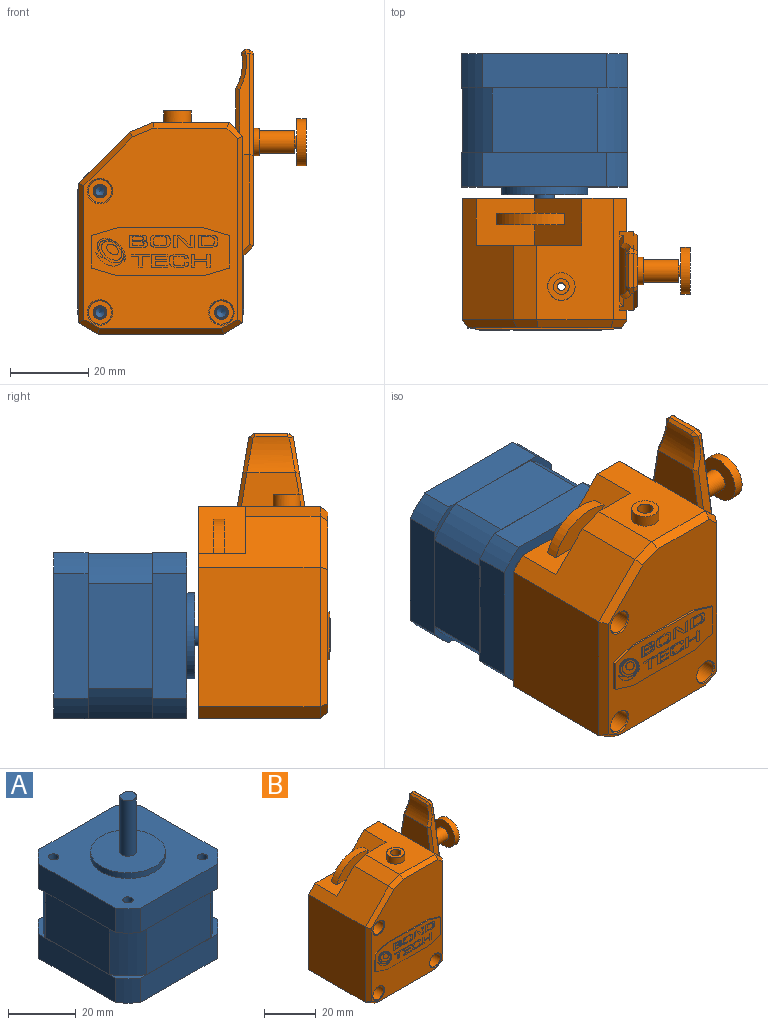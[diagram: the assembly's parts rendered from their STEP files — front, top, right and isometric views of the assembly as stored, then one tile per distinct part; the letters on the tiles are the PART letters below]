
ASSEMBLY  parts=2 mates=1
PART A: 50 faces, bbox 42.4x42.4x56 mm
  f0: cylinder r=2.5mm len=20mm, axis (0,0,-1), area 265.9mm2, adj f1,f2,f29,f30
  f1: plane 5x4.5mm, normal (0,0,1), area 18.6mm2, adj f0,f29
  f2: plane 22x22mm, normal (0,0,1), area 360.5mm2, adj f0,f3
  f3: cylinder r=11mm len=22mm, axis (0,0,-1), area 138.2mm2, adj f2,f8
  f4: plane 31.78x8.75mm, normal (1,0,0), area 278mm2, adj f8,f9,f10,f32
  f5: plane 31.78x8.75mm, normal (0,-1,0), area 278mm2, adj f8,f9,f11,f32
  f6: plane 31.78x8.75mm, normal (-1,0,0), area 278mm2, adj f8,f11,f12,f32
  f7: plane 31.78x8.75mm, normal (0,1,0), area 278mm2, adj f8,f10,f12,f32
  f8: plane 42.42x42.42mm, normal (0,0,1), area 1339.6mm2, adj f3,f4,f5,f6,f7,f9,f10,f11
  f9: cylinder r=26.5mm len=8.75mm, axis (0,0,-1), area 66.1mm2, adj f4,f5,f8,f32
  f10: cylinder r=26.5mm len=8.75mm, axis (0,0,-1), area 66.1mm2, adj f4,f7,f8,f32
  f11: cylinder r=26.5mm len=8.75mm, axis (0,0,-1), area 66.1mm2, adj f5,f6,f8,f32
  f12: cylinder r=26.5mm len=8.75mm, axis (0,0,-1), area 66.1mm2, adj f6,f7,f8,f32
  f13: cone r=1.25mm half-angle=59deg, axis (0,0,1), area 5.7mm2, adj f14
  f14: cylinder r=1.25mm len=2.5mm, axis (0,0,1), area 11.8mm2, adj f13,f15
  f15: plane 3x3mm, normal (0,0,1), area 2.2mm2, adj f14,f16
  f16: cylinder r=1.5mm len=6mm, axis (0,0,1), area 56.5mm2, adj f8,f15
  f17: cone r=1.25mm half-angle=59deg, axis (0,0,1), area 5.7mm2, adj f18
  f18: cylinder r=1.25mm len=2.5mm, axis (0,0,1), area 11.8mm2, adj f17,f19
  f19: plane 3x3mm, normal (0,0,1), area 2.2mm2, adj f18,f20
  f20: cylinder r=1.5mm len=6mm, axis (0,0,1), area 56.5mm2, adj f8,f19
  f21: cone r=1.25mm half-angle=59deg, axis (0,0,1), area 5.7mm2, adj f22
  f22: cylinder r=1.25mm len=2.5mm, axis (0,0,1), area 11.8mm2, adj f21,f23
  f23: plane 3x3mm, normal (0,0,1), area 2.2mm2, adj f22,f24
  f24: cylinder r=1.5mm len=6mm, axis (0,0,1), area 56.5mm2, adj f8,f23
  f25: cone r=1.25mm half-angle=59deg, axis (0,0,1), area 5.7mm2, adj f26
  f26: cylinder r=1.25mm len=2.5mm, axis (0,0,1), area 11.8mm2, adj f25,f27
  f27: plane 3x3mm, normal (0,0,1), area 2.2mm2, adj f26,f28
  f28: cylinder r=1.5mm len=6mm, axis (0,0,1), area 56.5mm2, adj f8,f27
  f29: plane 15x3mm, normal (0,1,0), area 45mm2, adj f0,f1,f30
  f30: plane 3x0.5mm, normal (0,0,1), area 1mm2, adj f0,f29
  f31: plane 42.42x42.42mm, normal (0,0,1), area 67.2mm2, adj f33,f34,f35,f36,f37,f38,f39,f40
  f32: plane 42.42x42.42mm, normal (0,0,-1), area 67.2mm2, adj f4,f5,f6,f7,f9,f10,f11,f12
  f33: cylinder r=25mm len=16.5mm, axis (0,0,1), area 181.5mm2, adj f31,f32,f34,f40
  f34: plane 26.79x16.5mm, normal (0,1,0), area 442mm2, adj f31,f32,f33,f35
  f35: cylinder r=25mm len=16.5mm, axis (0,0,1), area 181.5mm2, adj f31,f32,f34,f36
  f36: plane 26.79x16.5mm, normal (1,0,0), area 442mm2, adj f31,f32,f35,f37
  f37: cylinder r=25mm len=16.5mm, axis (0,0,1), area 181.5mm2, adj f31,f32,f36,f38
  f38: plane 26.79x16.5mm, normal (0,-1,0), area 442mm2, adj f31,f32,f37,f39
  f39: cylinder r=25mm len=16.5mm, axis (0,0,1), area 181.5mm2, adj f31,f32,f38,f40
  f40: plane 26.79x16.5mm, normal (-1,0,0), area 442mm2, adj f31,f32,f33,f39
  f41: plane 42.42x42.42mm, normal (0,0,-1), area 1748.1mm2, adj f42,f43,f44,f45,f46,f47,f48,f49
  f42: cylinder r=26.5mm len=8.75mm, axis (0,0,-1), area 66.1mm2, adj f31,f41,f48,f49
  f43: cylinder r=26.5mm len=8.75mm, axis (0,0,-1), area 66.1mm2, adj f31,f41,f47,f48
  f44: cylinder r=26.5mm len=8.75mm, axis (0,0,-1), area 66.1mm2, adj f31,f41,f46,f47
  f45: cylinder r=26.5mm len=8.75mm, axis (0,0,-1), area 66.1mm2, adj f31,f41,f46,f49
  f46: plane 31.78x8.75mm, normal (0,1,0), area 278mm2, adj f31,f41,f44,f45
  f47: plane 31.78x8.75mm, normal (-1,0,0), area 278mm2, adj f31,f41,f43,f44
  f48: plane 31.78x8.75mm, normal (0,-1,0), area 278mm2, adj f31,f41,f42,f43
  f49: plane 31.78x8.75mm, normal (1,0,0), area 278mm2, adj f31,f41,f42,f45
PART B: 276 faces, bbox 58.2x33.6x72.9 mm
  f0: cone r=3mm half-angle=45deg, axis (0,-1,0), area 6.9mm2, adj f4,f23
  f1: cone r=3mm half-angle=45deg, axis (0,-1,0), area 6.9mm2, adj f3,f23
  f2: cone r=3mm half-angle=45deg, axis (0,-1,0), area 6.9mm2, adj f5,f23
  f3: cylinder r=3mm len=6mm, axis (0,-1,0), area 80.1mm2, adj f1,f92
  f4: cylinder r=3mm len=6mm, axis (0,-1,0), area 80.1mm2, adj f0,f91
  f5: cylinder r=3mm len=6mm, axis (0,-1,0), area 80.1mm2, adj f2,f90
  f6: cylinder r=11mm len=22mm, axis (0,1,0), area 138.2mm2, adj f29,f89
  f7: cylinder r=1.75mm len=10.5mm, axis (-1,0,0), area 115.5mm2, adj f85,f88
  f8: cylinder r=1.5mm len=11mm, axis (-1,0,0), area 103.7mm2, adj f87,f88
  f9: cylinder r=6mm len=12mm, axis (-1,0,0), area 94.2mm2, adj f86,f87
  f10: cylinder r=2.88mm len=9mm, axis (-1,0,0), area 162.6mm2, adj f84,f85
  f11: cylinder r=3.5mm len=7mm, axis (-1,0,0), area 33mm2, adj f56,f84
  f12: cylinder r=2mm len=4mm, axis (0,0,-1), area 37.7mm2, adj f22,f52
  f13: cylinder r=3.5mm len=7mm, axis (0,0,-1), area 66mm2, adj f27,f52
  f14: cylinder r=1mm len=51mm, axis (0,0,-1), area 320.4mm2, adj f22,f51
  f15: cylinder r=8mm len=16mm, axis (0,0,-1), area 150.8mm2, adj f25,f51
  f16: cylinder r=1.75mm len=28.5mm, axis (0,1,0), area 313.4mm2, adj f29,f90
  f17: cylinder r=1.75mm len=28.5mm, axis (0,1,0), area 313.4mm2, adj f29,f91
  f18: cylinder r=1.75mm len=28.5mm, axis (0,1,0), area 313.4mm2, adj f29,f92
  f19: plane 35.32x12.32mm, normal (0,-1,0), area 302.9mm2, adj f43,f44,f45,f46,f47,f48,f49,f50
  f20: plane 15x12mm, normal (0,0,1), area 150.6mm2, adj f21,f28,f29,f93,f94,f95,f96
  f21: plane 12x12mm, normal (-0.71,0,0.71), area 171.1mm2, adj f20,f27,f29,f93,f94,f95,f96
  f22: plane 4x4mm, normal (0,0,1), area 9.4mm2, adj f12,f14
  f23: plane 51.2x39.2mm, normal (0,-1,0), area 1375.8mm2, adj f0,f1,f2,f34,f35,f36,f37,f38
  f24: plane 35.61x31mm, normal (-1,0,0), area 1104mm2, adj f28,f29,f33,f40
  f25: plane 32x31mm, normal (0,0,-1), area 790.9mm2, adj f15,f29,f32,f33,f41
  f26: plane 47.61x31mm, normal (1,0,0), area 863.4mm2, adj f29,f30,f32,f37,f53,f54,f55,f61
  f27: plane 31x19.5mm, normal (0,0,1), area 428mm2, adj f13,f21,f29,f30,f31,f34,f93
  f28: plane 31x13.03mm, normal (-0.71,0,0.71), area 409.4mm2, adj f20,f24,f29,f31,f38,f93
  f29: plane 54x42mm, normal (0,1,0), area 1538.3mm2, adj f6,f16,f17,f18,f20,f21,f24,f25
  f30: plane 31x3.5mm, normal (0.71,0,0.71), area 104mm2, adj f26,f27,f29,f35,f59,f60,f61,f62
  f31: plane 19x5.98mm, normal (-0.38,0,0.92), area 122.9mm2, adj f27,f28,f36,f93
  f32: plane 31x5mm, normal (0.5,0,-0.87), area 179mm2, adj f25,f26,f29,f39
  f33: plane 31x5mm, normal (-0.5,0,-0.87), area 179mm2, adj f24,f25,f29,f42
  f34: plane 19.5x2mm, normal (0,-0.57,0.82), area 46.6mm2, adj f23,f27,f35,f36
  f35: plane 4.08x4.08mm, normal (0.58,-0.57,0.58), area 10.7mm2, adj f23,f30,f34,f37
  f36: plane 6.25x3.66mm, normal (-0.31,-0.57,0.76), area 15.1mm2, adj f23,f31,f34,f38
  f37: plane 47.61x2mm, normal (0.82,-0.57,0), area 114.6mm2, adj f23,f26,f35,f39
  f38: plane 13.82x13.61mm, normal (-0.58,-0.57,0.58), area 43.9mm2, adj f23,f28,f36,f40
  f39: plane 5.38x3.7mm, normal (0.41,-0.57,-0.71), area 12.7mm2, adj f23,f32,f37,f41
  f40: plane 35.61x2mm, normal (-0.82,-0.57,0), area 85.3mm2, adj f23,f24,f38,f42
  f41: plane 32x2mm, normal (0,-0.57,-0.82), area 77.2mm2, adj f23,f25,f39,f42
  f42: plane 5.38x3.7mm, normal (-0.41,-0.57,-0.71), area 12.7mm2, adj f23,f33,f40,f41
  f43: plane 6.66x2mm, normal (-0.29,0,-0.96), area 3.5mm2, adj f19,f23,f44,f50
  f44: plane 21.99x0.5mm, normal (0,0,-1), area 11mm2, adj f19,f23,f43,f45
  f45: plane 6.66x2mm, normal (0.29,0,-0.96), area 3.5mm2, adj f19,f23,f44,f46
  f46: plane 8.3x0.5mm, normal (1,0,0), area 4.2mm2, adj f19,f23,f45,f47
  f47: plane 6.66x2mm, normal (0.29,0,0.96), area 3.5mm2, adj f19,f23,f46,f48
  f48: plane 21.99x0.5mm, normal (0,0,1), area 11mm2, adj f19,f23,f47,f49
  f49: plane 6.66x2mm, normal (-0.29,0,0.96), area 3.5mm2, adj f19,f23,f48,f50
  f50: plane 8.3x0.5mm, normal (-1,0,0), area 4.2mm2, adj f19,f23,f43,f49
  f51: plane 16x16mm, normal (0,0,-1), area 197.9mm2, adj f14,f15
  f52: plane 7x7mm, normal (0,0,1), area 25.9mm2, adj f12,f13
  f53: plane 24.54x1.7mm, normal (0,-1,0), area 40.3mm2, adj f26,f65,f82,f83
  f54: plane 24.54x1.7mm, normal (0,1,0), area 40.3mm2, adj f26,f62,f75,f76
  f55: plane 18x2.7mm, normal (0.71,0,-0.71), area 68.7mm2, adj f26,f56,f75,f83
  f56: plane 49.25x18mm, normal (1,0,0), area 734.7mm2, adj f11,f55,f76,f77,f78,f79,f80,f81
  f57: plane 8.85x1.28mm, normal (0,0,1), area 11.1mm2, adj f66,f67,f70,f71,f72,f79
  f58: cylinder r=13.85mm len=12.41mm, axis (0,1,0), area 103.5mm2, adj f59,f68,f69,f70,f71,f72,f73,f74
  f59: plane 15.8x10.33mm, normal (-1,0,0), area 145.5mm2, adj f30,f58,f68,f74
  f60: plane 6.55x1.09mm, normal (1,0,0), area 3.6mm2, adj f30,f61,f62
  f61: plane 6.55x1.8mm, normal (0,-1,0), area 10.2mm2, adj f26,f30,f60,f62
  f62: plane 25.8x4.28mm, normal (0,0.99,0.16), area 59.8mm2, adj f30,f54,f60,f61,f66,f73,f74,f77
  f63: plane 6.55x1.09mm, normal (1,0,0), area 3.6mm2, adj f30,f64,f65
  f64: plane 6.55x1.8mm, normal (0,1,0), area 10.2mm2, adj f26,f30,f63,f65
  f65: plane 26.01x4.32mm, normal (0,-0.99,0.16), area 60mm2, adj f30,f53,f63,f64,f67,f68,f69,f81
  f66: plane 1.26x1.22mm, normal (0,0.71,0.71), area 1.9mm2, adj f57,f62,f72,f73,f78
  f67: plane 1.38x1.24mm, normal (0,-0.58,0.81), area 1.9mm2, adj f57,f65,f69,f70,f80
  f68: plane 11.38x2.9mm, normal (-0.71,-0.7,0.12), area 15.5mm2, adj f30,f58,f59,f65,f69
  f69: bspline ~9.52x2.69mm, area 13.8mm2, adj f58,f65,f67,f68,f70
  f70: bspline ~1.95x1.78mm, area 1.4mm2, adj f57,f58,f67,f69,f71
  f71: plane 8.79x0.83mm, normal (-0.71,0,0.71), area 9.7mm2, adj f57,f58,f70,f72
  f72: bspline ~1.96x1.86mm, area 1.4mm2, adj f57,f58,f66,f71,f73
  f73: bspline ~9.42x2.69mm, area 13.7mm2, adj f58,f62,f66,f72,f74
  f74: plane 11.38x2.9mm, normal (-0.71,0.7,0.12), area 15.5mm2, adj f30,f58,f59,f62,f73
  f75: plane 3.11x2.7mm, normal (0.5,0.71,-0.5), area 4.4mm2, adj f26,f54,f55,f76
  f76: plane 23.25x1mm, normal (0.71,0.71,0), area 32.5mm2, adj f54,f56,f75,f77
  f77: plane 25.88x5.22mm, normal (0.71,0.7,0.12), area 36.7mm2, adj f56,f62,f76,f78
  f78: plane 1.68x1.61mm, normal (0.71,0.5,0.5), area 1.9mm2, adj f56,f66,f77,f79
  f79: plane 8.82x1mm, normal (0.71,0,0.71), area 12mm2, adj f56,f57,f78,f80
  f80: plane 1.7x1.56mm, normal (0.71,-0.41,0.58), area 1.9mm2, adj f56,f67,f79,f81
  f81: plane 26.09x5.24mm, normal (0.71,-0.7,0.12), area 36.9mm2, adj f56,f65,f80,f82
  f82: plane 23.25x1mm, normal (0.71,-0.71,0), area 32.5mm2, adj f53,f56,f81,f83
  f83: plane 3.11x2.7mm, normal (0.5,-0.71,-0.5), area 4.4mm2, adj f26,f53,f55,f82
  f84: plane 7x7mm, normal (1,0,0), area 12.5mm2, adj f10,f11
  f85: plane 5.75x5.75mm, normal (1,0,0), area 16.3mm2, adj f7,f10
  f86: plane 12x12mm, normal (1,0,0), area 113.1mm2, adj f9
  f87: plane 12x12mm, normal (-1,0,0), area 106mm2, adj f8,f9
  f88: plane 3.5x3.5mm, normal (1,0,0), area 2.6mm2, adj f7,f8
  f89: plane 22x22mm, normal (0,1,0), area 380.1mm2, adj f6
  f90: plane 6x6mm, normal (0,-1,0), area 18.7mm2, adj f5,f16
  f91: plane 6x6mm, normal (0,-1,0), area 18.7mm2, adj f4,f17
  f92: plane 6x6mm, normal (0,-1,0), area 18.7mm2, adj f3,f18
  f93: plane 27x12mm, normal (0,1,0), area 175.7mm2, adj f20,f21,f27,f28,f31
  f94: cylinder r=13mm len=17.46mm, axis (0,1,0), area 64.2mm2, adj f20,f21,f95,f96
  f95: plane 17.46x8.75mm, normal (0,-1,0), area 92.5mm2, adj f20,f21,f94
  f96: plane 17.46x8.75mm, normal (0,1,0), area 92.5mm2, adj f20,f21,f94
  f97: extruded ~1.11x0.12mm, area 0.1mm2, adj f19,f98,f105,f106
  f98: extruded ~0.75x0.1mm, area 0.1mm2, adj f19,f97,f99,f106
  f99: extruded ~1.46x0.61mm, area 0.2mm2, adj f19,f98,f100,f106
  f100: extruded ~2.8x1.93mm, area 0.4mm2, adj f19,f99,f101,f106
  f101: extruded ~2.12x0.3mm, area 0.2mm2, adj f19,f100,f102,f106
  f102: extruded ~0.61x0.21mm, area 0.1mm2, adj f19,f101,f103,f106
  f103: extruded ~2.24x0.4mm, area 0.2mm2, adj f19,f102,f104,f106
  f104: extruded ~1.92x1.61mm, area 0.3mm2, adj f19,f103,f105,f106
  f105: extruded ~1.55x0.73mm, area 0.2mm2, adj f19,f97,f104,f106
  f106: plane 5.64x4.71mm, normal (0,-1,0), area 1.5mm2, adj f97,f98,f99,f100,f101,f102,f103,f104
  f107: plane 5.29x4.97mm, normal (0,-1,0), area 12.8mm2, adj f108,f109,f110,f111,f112,f113,f114,f115
  f108: extruded ~1.65x0.26mm, area 0.2mm2, adj f19,f107,f109,f114
  f109: extruded ~1.38x0.67mm, area 0.2mm2, adj f19,f107,f108,f110
  f110: extruded ~2.07x1.1mm, area 0.2mm2, adj f19,f107,f109,f111
  f111: extruded ~2.25x1.17mm, area 0.3mm2, adj f19,f107,f110,f112
  f112: extruded ~1.59x0.62mm, area 0.2mm2, adj f19,f107,f111,f113
  f113: extruded ~1.64x0.27mm, area 0.2mm2, adj f19,f107,f112,f114
  f114: extruded ~2.81x2.58mm, area 0.4mm2, adj f19,f107,f108,f113
  f115: extruded ~1.83x1.74mm, area 0.3mm2, adj f107,f116,f118,f119
  f116: extruded ~1.18x1.1mm, area 0.2mm2, adj f107,f115,f117,f119
  f117: extruded ~1.65x1.53mm, area 0.2mm2, adj f107,f116,f118,f119
  f118: extruded ~1.24x0.98mm, area 0.2mm2, adj f107,f115,f117,f119
  f119: plane 3.1x2.91mm, normal (0,-1,0), area 5.8mm2, adj f115,f116,f117,f118
  f120: extruded ~2.04x0.25mm, area 0.2mm2, adj f19,f121,f128,f129
  f121: extruded ~1.51x1mm, area 0.2mm2, adj f19,f120,f122,f129
  f122: extruded ~1.54x0.45mm, area 0.2mm2, adj f19,f121,f123,f129
  f123: extruded ~1.53x1.38mm, area 0.2mm2, adj f19,f122,f124,f129
  f124: extruded ~2.62x1.38mm, area 0.3mm2, adj f19,f123,f125,f129
  f125: extruded ~1.35x0.54mm, area 0.1mm2, adj f19,f124,f126,f129
  f126: extruded ~1.29x0.51mm, area 0.1mm2, adj f19,f125,f127,f129
  f127: extruded ~1.46x0.16mm, area 0.1mm2, adj f19,f126,f128,f129
  f128: extruded ~0.71x0.2mm, area 0.1mm2, adj f19,f120,f127,f129
  f129: plane 4.88x3.75mm, normal (0,-1,0), area 2.3mm2, adj f120,f121,f122,f123,f124,f125,f126,f127
  f130: extruded ~1.42x0.34mm, area 0.1mm2, adj f19,f131,f137,f138
  f131: extruded ~2.39x1.09mm, area 0.3mm2, adj f19,f130,f132,f138
  f132: extruded ~2.4x1.57mm, area 0.3mm2, adj f19,f131,f133,f138
  f133: extruded ~0.95x0.44mm, area 0.1mm2, adj f19,f132,f134,f138
  f134: extruded ~3.9x2.5mm, area 0.5mm2, adj f19,f133,f135,f138
  f135: extruded ~1.7x0.45mm, area 0.2mm2, adj f19,f134,f136,f138
  f136: extruded ~2.49x0.99mm, area 0.3mm2, adj f19,f135,f137,f138
  f137: extruded ~1.82x0.79mm, area 0.2mm2, adj f19,f130,f136,f138
  f138: plane 7.09x3.47mm, normal (0,-1,0), area 5.7mm2, adj f130,f131,f132,f133,f134,f135,f136,f137
  f139: plane 4.65x3.15mm, normal (0,-1,0), area 8.6mm2, adj f140,f141,f142,f143,f144,f145,f146,f147
  f140: extruded ~1.23x0.11mm, area 0.1mm2, adj f19,f139,f141,f149
  f141: plane 2.74x0.1mm, normal (0,0,1), area 0.3mm2, adj f19,f139,f140,f142
  f142: plane 3.15x0.1mm, normal (-1,0,0), area 0.3mm2, adj f19,f139,f141,f143
  f143: plane 2.95x0.1mm, normal (0,0,-1), area 0.3mm2, adj f19,f139,f142,f144
  f144: extruded ~1.11x0.11mm, area 0.1mm2, adj f19,f139,f143,f145
  f145: extruded ~0.77x0.59mm, area 0.1mm2, adj f19,f139,f144,f146
  f146: extruded ~0.97x0.75mm, area 0.1mm2, adj f19,f139,f145,f147
  f147: plane 0.1x0.01mm, normal (1,0,0), area 0mm2, adj f19,f139,f146,f148
  f148: extruded ~0.81x0.68mm, area 0.1mm2, adj f19,f139,f147,f149
  f149: extruded ~0.72x0.52mm, area 0.1mm2, adj f19,f139,f140,f148
  f150: extruded ~0.88x0.1mm, area 0.1mm2, adj f139,f151,f156,f165
  f151: extruded ~0.43x0.28mm, area 0.1mm2, adj f139,f150,f152,f165
  f152: extruded ~0.42x0.33mm, area 0.1mm2, adj f139,f151,f153,f165
  f153: extruded ~0.62x0.1mm, area 0.1mm2, adj f139,f152,f154,f165
  f154: plane 1.75x0.1mm, normal (0,0,-1), area 0.2mm2, adj f139,f153,f155,f165
  f155: plane 0.95x0.1mm, normal (1,0,0), area 0.1mm2, adj f139,f154,f156,f165
  f156: plane 1.54x0.1mm, normal (0,0,1), area 0.2mm2, adj f139,f150,f155,f165
  f157: extruded ~1.25x0.1mm, area 0.1mm2, adj f139,f158,f163,f164
  f158: extruded ~0.42x0.3mm, area 0.1mm2, adj f139,f157,f159,f164
  f159: extruded ~0.48x0.36mm, area 0.1mm2, adj f139,f158,f160,f164
  f160: extruded ~0.94x0.1mm, area 0.1mm2, adj f139,f159,f161,f164
  f161: plane 1.55x0.1mm, normal (0,0,-1), area 0.2mm2, adj f139,f160,f162,f164
  f162: plane 1.01x0.1mm, normal (1,0,0), area 0.1mm2, adj f139,f161,f163,f164
  f163: plane 1.31x0.1mm, normal (0,0,1), area 0.1mm2, adj f139,f157,f162,f164
  f164: plane 2.85x1.01mm, normal (0,-1,0), area 2.8mm2, adj f157,f158,f159,f160,f161,f162,f163
  f165: plane 2.7x0.95mm, normal (0,-1,0), area 2.5mm2, adj f150,f151,f152,f153,f154,f155,f156
  f166: plane 5.11x3.21mm, normal (0,-1,0), area 7.5mm2, adj f167,f168,f169,f170,f171,f172,f173,f174
  f167: extruded ~2.17x0.35mm, area 0.2mm2, adj f19,f166,f168,f173
  f168: extruded ~0.8x0.55mm, area 0.1mm2, adj f19,f166,f167,f169
  f169: extruded ~3.27x0.11mm, area 0.3mm2, adj f19,f166,f168,f170
  f170: extruded ~0.83x0.56mm, area 0.1mm2, adj f19,f166,f169,f171
  f171: extruded ~1.73x0.11mm, area 0.2mm2, adj f19,f166,f170,f172
  f172: extruded ~0.83x0.7mm, area 0.1mm2, adj f19,f166,f171,f173
  f173: extruded ~3.87x0.37mm, area 0.4mm2, adj f19,f166,f167,f172
  f174: extruded ~0.66x0.42mm, area 0.1mm2, adj f166,f175,f182,f183
  f175: extruded ~1.32x0.1mm, area 0.1mm2, adj f166,f174,f176,f183
  f176: extruded ~1.47x0.33mm, area 0.2mm2, adj f166,f175,f177,f183
  f177: extruded ~0.87x0.1mm, area 0.1mm2, adj f166,f176,f178,f183
  f178: extruded ~1.05x0.28mm, area 0.1mm2, adj f166,f177,f179,f183
  f179: extruded ~1.38x0.14mm, area 0.1mm2, adj f166,f178,f180,f183
  f180: extruded ~1.28x0.1mm, area 0.1mm2, adj f166,f179,f181,f183
  f181: extruded ~0.65x0.36mm, area 0.1mm2, adj f166,f180,f182,f183
  f182: plane 0.88x0.1mm, normal (-1,0,0), area 0.1mm2, adj f166,f174,f181,f183
  f183: plane 3.31x2.38mm, normal (0,-1,0), area 7.4mm2, adj f174,f175,f176,f177,f178,f179,f180,f181
  f184: extruded ~0.81x0.77mm, area 0.1mm2, adj f19,f185,f199,f200
  f185: plane 2.06x1.93mm, normal (-0.68,0,-0.73), area 0.3mm2, adj f19,f184,f186,f200
  f186: plane 1.5x0.1mm, normal (0,0,-1), area 0.2mm2, adj f19,f185,f187,f200
  f187: plane 3.15x0.1mm, normal (1,0,0), area 0.3mm2, adj f19,f186,f188,f200
  f188: plane 0.9x0.1mm, normal (0,0,1), area 0.1mm2, adj f19,f187,f189,f200
  f189: plane 2.1x0.1mm, normal (-1,0,0), area 0.2mm2, adj f19,f188,f190,f200
  f190: extruded ~0.65x0.1mm, area 0.1mm2, adj f19,f189,f191,f200
  f191: plane 0.1x0.03mm, normal (0,0,1), area 0mm2, adj f19,f190,f192,f200
  f192: extruded ~1.01x1.01mm, area 0.1mm2, adj f19,f191,f193,f200
  f193: plane 1.82x1.74mm, normal (0.69,0,0.72), area 0.3mm2, adj f19,f192,f194,f200
  f194: plane 1.49x0.1mm, normal (0,0,1), area 0.1mm2, adj f19,f193,f195,f200
  f195: plane 3.15x0.1mm, normal (-1,0,0), area 0.3mm2, adj f19,f194,f196,f200
  f196: plane 0.89x0.1mm, normal (0,0,-1), area 0.1mm2, adj f19,f195,f197,f200
  f197: plane 2.08x0.1mm, normal (1,0,0), area 0.2mm2, adj f19,f196,f198,f200
  f198: extruded ~0.66x0.1mm, area 0.1mm2, adj f19,f197,f199,f200
  f199: plane 0.1x0.04mm, normal (0,0,-1), area 0mm2, adj f19,f184,f198,f200
  f200: plane 5.23x3.15mm, normal (0,-1,0), area 8.8mm2, adj f184,f185,f186,f187,f188,f189,f190,f191
  f201: plane 4.98x3.15mm, normal (0,-1,0), area 7.9mm2, adj f202,f203,f204,f205,f206,f207,f208,f209
  f202: extruded ~1.65x0.27mm, area 0.2mm2, adj f19,f201,f203,f209
  f203: plane 2.79x0.1mm, normal (0,0,1), area 0.3mm2, adj f19,f201,f202,f204
  f204: plane 3.15x0.1mm, normal (-1,0,0), area 0.3mm2, adj f19,f201,f203,f205
  f205: plane 2.9x0.1mm, normal (0,0,-1), area 0.3mm2, adj f19,f201,f204,f206
  f206: extruded ~0.81x0.1mm, area 0.1mm2, adj f19,f201,f205,f207
  f207: extruded ~0.98x0.4mm, area 0.1mm2, adj f19,f201,f206,f208
  f208: extruded ~1.33x0.29mm, area 0.1mm2, adj f19,f201,f207,f209
  f209: extruded ~1.1x0.54mm, area 0.1mm2, adj f19,f201,f202,f208
  f210: extruded ~1.15x0.19mm, area 0.1mm2, adj f201,f211,f216,f217
  f211: extruded ~0.94x0.29mm, area 0.1mm2, adj f201,f210,f212,f217
  f212: extruded ~0.99x0.27mm, area 0.1mm2, adj f201,f211,f213,f217
  f213: extruded ~1.07x0.19mm, area 0.1mm2, adj f201,f212,f214,f217
  f214: plane 1.84x0.1mm, normal (0,0,-1), area 0.2mm2, adj f201,f213,f215,f217
  f215: plane 2.32x0.1mm, normal (1,0,0), area 0.2mm2, adj f201,f214,f216,f217
  f216: plane 1.74x0.1mm, normal (0,0,1), area 0.2mm2, adj f201,f210,f215,f217
  f217: plane 3.18x2.32mm, normal (0,-1,0), area 7mm2, adj f210,f211,f212,f213,f214,f215,f216
  f218: extruded ~0.78x0.36mm, area 0.1mm2, adj f19,f219,f239,f240
  f219: plane 0.11x0.1mm, normal (1,0,0), area 0mm2, adj f19,f218,f220,f240
  f220: plane 0.9x0.1mm, normal (0,0,1), area 0.1mm2, adj f19,f219,f221,f240
  f221: cylinder r=0.76mm len=0.15mm, axis (0,1,0), area 0mm2, adj f19,f220,f222,f240
  f222: extruded ~1.53x0.55mm, area 0.2mm2, adj f19,f221,f223,f240
  f223: extruded ~1.33x0.25mm, area 0.1mm2, adj f19,f222,f224,f240
  f224: extruded ~1.24x0.16mm, area 0.1mm2, adj f19,f223,f225,f240
  f225: extruded ~0.77x0.26mm, area 0.1mm2, adj f19,f224,f226,f240
  f226: extruded ~1.48x0.13mm, area 0.1mm2, adj f19,f225,f227,f240
  f227: extruded ~1.06x0.16mm, area 0.1mm2, adj f19,f226,f228,f240
  f228: extruded ~0.46x0.13mm, area 0mm2, adj f19,f227,f229,f240
  f229: plane 0.9x0.1mm, normal (0,0,-1), area 0.1mm2, adj f19,f228,f230,f240
  f230: extruded ~0.35x0.1mm, area 0mm2, adj f19,f229,f231,f240
  f231: extruded ~0.57x0.56mm, area 0.1mm2, adj f19,f230,f232,f240
  f232: extruded ~1.4x0.12mm, area 0.1mm2, adj f19,f231,f233,f240
  f233: extruded ~1.29x0.1mm, area 0.1mm2, adj f19,f232,f234,f240
  f234: extruded ~1.31x0.48mm, area 0.1mm2, adj f19,f233,f235,f240
  f235: extruded ~0.79x0.18mm, area 0.1mm2, adj f19,f234,f236,f240
  f236: extruded ~0.86x0.1mm, area 0.1mm2, adj f19,f235,f237,f240
  f237: extruded ~0.87x0.61mm, area 0.1mm2, adj f19,f236,f238,f240
  f238: extruded ~1.77x0.18mm, area 0.2mm2, adj f19,f237,f239,f240
  f239: extruded ~2.07x0.23mm, area 0.2mm2, adj f19,f218,f238,f240
  f240: plane 4.84x3.21mm, normal (0,-1,0), area 6.6mm2, adj f218,f219,f220,f221,f222,f223,f224,f225
  f241: plane 2.72x0.1mm, normal (1,0,0), area 0.3mm2, adj f19,f242,f248,f249
  f242: plane 1.82x0.1mm, normal (0,0,-1), area 0.2mm2, adj f19,f241,f243,f249
  f243: plane 0.44x0.1mm, normal (1,0,0), area 0mm2, adj f19,f242,f244,f249
  f244: plane 4.51x0.1mm, normal (0,0,1), area 0.5mm2, adj f19,f243,f245,f249
  f245: plane 0.44x0.1mm, normal (-1,0,0), area 0mm2, adj f19,f244,f246,f249
  f246: plane 1.79x0.1mm, normal (0,0,-1), area 0.2mm2, adj f19,f245,f247,f249
  f247: plane 2.72x0.1mm, normal (-1,0,0), area 0.3mm2, adj f19,f246,f248,f249
  f248: plane 0.9x0.1mm, normal (0,0,-1), area 0.1mm2, adj f19,f241,f247,f249
  f249: plane 4.51x3.15mm, normal (0,-1,0), area 4.4mm2, adj f241,f242,f243,f244,f245,f246,f247,f248
  f250: plane 0.94x0.1mm, normal (1,0,0), area 0.1mm2, adj f19,f251,f261,f262
  f251: plane 2.99x0.1mm, normal (0,0,-1), area 0.3mm2, adj f19,f250,f252,f262
  f252: plane 0.41x0.1mm, normal (1,0,0), area 0mm2, adj f19,f251,f253,f262
  f253: plane 3.88x0.1mm, normal (0,0,1), area 0.4mm2, adj f19,f252,f254,f262
  f254: plane 3.15x0.1mm, normal (-1,0,0), area 0.3mm2, adj f19,f253,f255,f262
  f255: plane 3.9x0.1mm, normal (0,0,-1), area 0.4mm2, adj f19,f254,f256,f262
  f256: plane 0.41x0.1mm, normal (1,0,0), area 0mm2, adj f19,f255,f257,f262
  f257: plane 3x0.1mm, normal (0,0,1), area 0.3mm2, adj f19,f256,f258,f262
  f258: plane 1.03x0.1mm, normal (1,0,0), area 0.1mm2, adj f19,f257,f259,f262
  f259: plane 2.85x0.1mm, normal (0,0,-1), area 0.3mm2, adj f19,f258,f260,f262
  f260: plane 0.37x0.1mm, normal (1,0,0), area 0mm2, adj f19,f259,f261,f262
  f261: plane 2.85x0.1mm, normal (0,0,1), area 0.3mm2, adj f19,f250,f260,f262
  f262: plane 3.9x3.15mm, normal (0,-1,0), area 6.3mm2, adj f250,f251,f252,f253,f254,f255,f256,f257
  f263: plane 3.15x0.1mm, normal (1,0,0), area 0.3mm2, adj f19,f264,f274,f275
  f264: plane 0.9x0.1mm, normal (0,0,1), area 0.1mm2, adj f19,f263,f265,f275
  f265: plane 1.34x0.1mm, normal (-1,0,0), area 0.1mm2, adj f19,f264,f266,f275
  f266: plane 3.07x0.1mm, normal (0,0,1), area 0.3mm2, adj f19,f265,f267,f275
  f267: plane 1.34x0.1mm, normal (1,0,0), area 0.1mm2, adj f19,f266,f268,f275
  f268: plane 0.9x0.1mm, normal (0,0,1), area 0.1mm2, adj f19,f267,f269,f275
  f269: plane 3.15x0.1mm, normal (-1,0,0), area 0.3mm2, adj f19,f268,f270,f275
  f270: plane 0.9x0.1mm, normal (0,0,-1), area 0.1mm2, adj f19,f269,f271,f275
  f271: plane 1.4x0.1mm, normal (1,0,0), area 0.1mm2, adj f19,f270,f272,f275
  f272: plane 3.07x0.1mm, normal (0,0,-1), area 0.3mm2, adj f19,f271,f273,f275
  f273: plane 1.4x0.1mm, normal (-1,0,0), area 0.1mm2, adj f19,f272,f274,f275
  f274: plane 0.9x0.1mm, normal (0,0,-1), area 0.1mm2, adj f19,f263,f273,f275
  f275: plane 4.86x3.15mm, normal (0,-1,0), area 6.9mm2, adj f263,f264,f265,f266,f267,f268,f269,f270
PLACE A rot(axis=(1,0,0),90deg) t=(23.26,40.32,13.97)mm
PLACE B t=(23.26,37.32,13.97)mm fixed
MATE fastened B.f0 <-> A.f25  axis (0,1,0) through (7.76,37.32,29.47)mm
